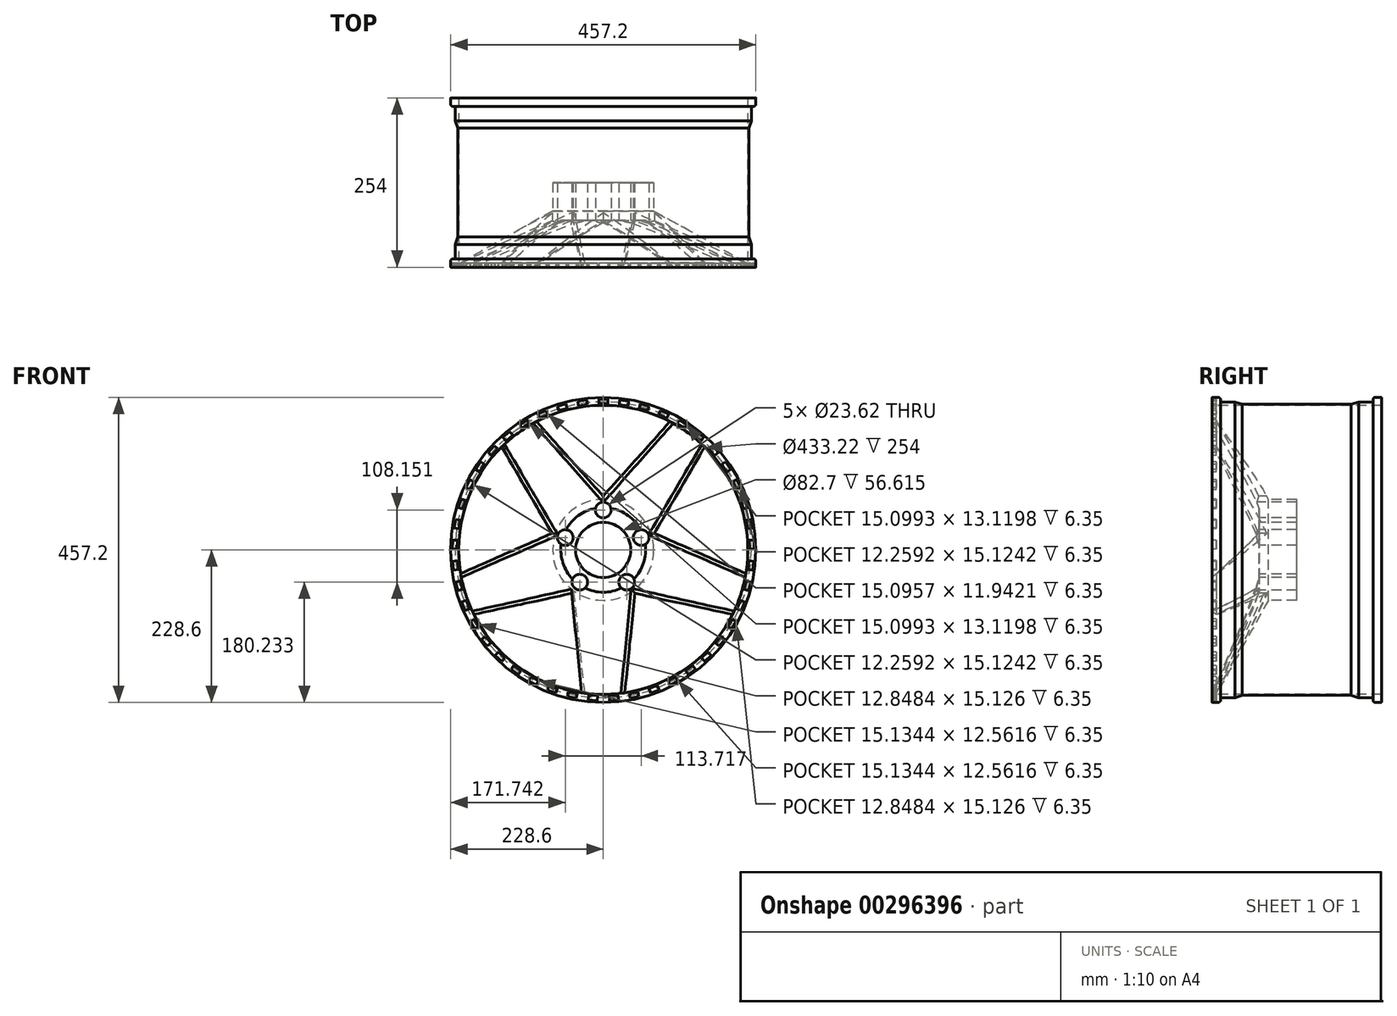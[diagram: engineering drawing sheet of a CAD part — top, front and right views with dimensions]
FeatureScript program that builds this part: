
annotation { "Feature Type Name" : "Feature", "Feature Type Description" : "" }
export const myFeature = defineFeature(function(context is Context, id is Id, definition is map)
    precondition{}
    {
        {
            var Q0;
            Q0=qCreatedBy(makeId("Right.planeOp"),FACE);
            var sketch = newSketch(context, id + "F0", { "sketchPlane" : qUnion([Q0])});
            skLineSegment(sketch, "E0", {"start": v(0, 0) * mm, "end": v(-56.62, 0) * mm});
            skLineSegment(sketch, "E1", {"start": v(0, 0) * mm, "end": v(0, 75.72) * mm});
            skLineSegment(sketch, "E2", {"start": v(0, 0) * mm, "end": v(0, 63.5) * mm});
            skLineSegment(sketch, "E3", {"start": v(-127, 216.61) * mm, "end": v(-127, 228.28) * mm});
            skLineSegment(sketch, "E4", {"start": v(-126.68, 228.6) * mm, "end": v(-117.48, 228.6) * mm});
            skLineSegment(sketch, "E5", {"start": v(-127, 216.61) * mm, "end": v(-56.62, 63.5) * mm});
            skLineSegment(sketch, "E6", {"start": v(-120.38, 216.61) * mm, "end": v(-42.61, 75.72) * mm});
            skLineSegment(sketch, "E7", {"start": v(-120.38, 216.61) * mm, "end": v(0, 216.61) * mm});
            skLineSegment(sketch, "E8", {"start": v(-114.3, 225.43) * mm, "end": v(-114.3, 223.38) * mm});
            skLineSegment(sketch, "E9", {"start": v(-112.78, 221.86) * mm, "end": v(-92.74, 221.86) * mm});
            skLineSegment(sketch, "E10", {"start": v(-92.74, 221.86) * mm, "end": v(-81.66, 218.09) * mm});
            skLineSegment(sketch, "E11", {"start": v(-81.66, 218.09) * mm, "end": v(0, 218.09) * mm});
            skPoint(sketch, "E12.visualSharp", {"position": v(-127, 228.6) * mm});
            skArc(sketch, "E12.filletArc", {"start": v(-126.68, 228.6) * mm, "mid": v(-126.9, 228.5) * mm, "end": v(-127, 228.28) * mm});
            skPoint(sketch, "E13.visualSharp", {"position": v(-114.3, 228.6) * mm});
            skArc(sketch, "E13.filletArc", {"start": v(-114.3, 225.43) * mm, "mid": v(-115.23, 227.67) * mm, "end": v(-117.48, 228.6) * mm});
            skPoint(sketch, "E14.visualSharp", {"position": v(-114.3, 221.86) * mm});
            skArc(sketch, "E14.filletArc", {"start": v(-114.3, 223.38) * mm, "mid": v(-113.85, 222.3) * mm, "end": v(-112.78, 221.86) * mm});
            skLineSegment(sketch, "E15", {"start": v(-56.62, 63.5) * mm, "end": v(-56.62, 0) * mm});
            skLineSegment(sketch, "E16", {"start": v(-56.62, 0) * mm, "end": v(0, 0) * mm});
            skLineSegment(sketch, "E17", {"start": v(-42.61, 75.72) * mm, "end": v(0, 75.72) * mm});
            skLineSegment(sketch, "E18", {"start": v(0, 75.72) * mm, "end": v(0, 63.5) * mm});
            skPoint(sketch, "E19.orphan", {"position": v(-35.86, 63.5) * mm});
            skPoint(sketch, "E20.orphan", {"position": v(0, 228.6) * mm});
            skLineSegment(sketch, "E21.MirrorCS", {"start": v(120.38, 216.61) * mm, "end": v(0, 216.61) * mm});
            skLineSegment(sketch, "E22.MirrorCS", {"start": v(127, 216.61) * mm, "end": v(127, 228.28) * mm});
            skLineSegment(sketch, "E23.MirrorCS", {"start": v(81.66, 218.09) * mm, "end": v(0, 218.09) * mm});
            skLineSegment(sketch, "E24.MirrorCS", {"start": v(92.74, 221.86) * mm, "end": v(81.66, 218.09) * mm});
            skLineSegment(sketch, "E25.MirrorCS", {"start": v(112.78, 221.86) * mm, "end": v(92.74, 221.86) * mm});
            skLineSegment(sketch, "E26.MirrorCS", {"start": v(126.68, 228.6) * mm, "end": v(117.48, 228.6) * mm});
            skArc(sketch, "E27.MirrorCS", {"start": v(114.3, 225.43) * mm, "mid": v(115.23, 227.67) * mm, "end": v(117.48, 228.6) * mm});
            skLineSegment(sketch, "E28.MirrorCS", {"start": v(114.3, 225.43) * mm, "end": v(114.3, 223.38) * mm});
            skArc(sketch, "E29.MirrorCS", {"start": v(114.3, 223.38) * mm, "mid": v(113.85, 222.3) * mm, "end": v(112.78, 221.86) * mm});
            skArc(sketch, "E30.MirrorCS", {"start": v(126.68, 228.6) * mm, "mid": v(126.9, 228.5) * mm, "end": v(127, 228.28) * mm});
            skLineSegment(sketch, "E31", {"start": v(127, 216.61) * mm, "end": v(120.38, 216.61) * mm});
            skLineSegment(sketch, "E32", {"start": v(-76.11, 0) * mm, "end": v(62.35, 0) * mm});
            skSolve(sketch);
        }
        {
            var Q0;
            Q0 = qSketchRegion(id + "F0", true);
            var Q1;
            Q1=sQuery(id+"F0.wireOp",EDGE,"E32");
            revolve(context, id + "F1", {"entities" : qUnion([Q0]), "axis" : qUnion([Q1]), "revolveType" : RevolveType.FULL});
        }
        {
            var Q0;
            Q0=makeQuery(id+"F1.opRevolve","SWEPT_FACE",FACE,{"disambiguationData":[OSD([sQuery(id+"F0.wireOp",EDGE,"E3")])]});
            var sketch = newSketch(context, id + "F2", { "sketchPlane" : qUnion([Q0])});
            skCircle(sketch, "E33", {"center": v(0, 59.78) * mm, "radius": 11.8 * mm});
            skCircle(sketch, "E34.1.0", {"center": v(-56.86, 18.47) * mm, "radius": 11.8 * mm});
            skCircle(sketch, "E34.2.0", {"center": v(-35.14, -48.37) * mm, "radius": 11.8 * mm});
            skCircle(sketch, "E34.3.0", {"center": v(35.14, -48.37) * mm, "radius": 11.8 * mm});
            skCircle(sketch, "E34.4.0", {"center": v(56.86, 18.47) * mm, "radius": 11.8 * mm});
            skPoint(sketch, "E34.center", {"position": v(0, 0) * mm});
            skCircle(sketch, "E35", {"center": v(0, 0) * mm, "radius": 41.35 * mm});
            skPoint(sketch, "E36.0.midPoint", {"position": v(0, -65.14) * mm});
            skLineSegment(sketch, "E37", {"start": v(47.33, -65.14) * mm, "end": v(32.25, -214.2) * mm});
            skLineSegment(sketch, "E38.MirrorCS", {"start": v(-47.33, -65.14) * mm, "end": v(-32.25, -214.2) * mm});
            skLineSegment(sketch, "E39.1.0", {"start": v(47.33, -65.14) * mm, "end": v(193.75, -96.86) * mm});
            skLineSegment(sketch, "E39.1.1", {"start": v(76.57, 24.88) * mm, "end": v(213.68, -35.52) * mm});
            skLineSegment(sketch, "E39.2.0", {"start": v(76.57, 24.88) * mm, "end": v(152, 154.33) * mm});
            skLineSegment(sketch, "E39.2.1", {"start": v(0, 80.52) * mm, "end": v(99.81, 192.24) * mm});
            skLineSegment(sketch, "E39.3.0", {"start": v(0, 80.52) * mm, "end": v(-99.81, 192.24) * mm});
            skLineSegment(sketch, "E39.3.1", {"start": v(-76.57, 24.88) * mm, "end": v(-152, 154.33) * mm});
            skLineSegment(sketch, "E39.4.0", {"start": v(-76.57, 24.88) * mm, "end": v(-213.68, -35.52) * mm});
            skLineSegment(sketch, "E39.4.1", {"start": v(-47.33, -65.14) * mm, "end": v(-193.75, -96.86) * mm});
            skArc(sketch, "E40", {"start": v(-152, 154.33) * mm, "mid": v(-206, 66.94) * mm, "end": v(-213.68, -35.52) * mm});
            skArc(sketch, "E41.trimOffspring", {"start": v(99.81, 192.24) * mm, "mid": v(0, 216.61) * mm, "end": v(-99.81, 192.24) * mm});
            skArc(sketch, "E42.trimOffspring", {"start": v(213.68, -35.52) * mm, "mid": v(206, 66.94) * mm, "end": v(152, 154.33) * mm});
            skArc(sketch, "E43.trimOffspring", {"start": v(32.25, -214.2) * mm, "mid": v(127.32, -175.24) * mm, "end": v(193.75, -96.86) * mm});
            skArc(sketch, "E44.trimOffspring", {"start": v(-193.75, -96.86) * mm, "mid": v(-127.32, -175.24) * mm, "end": v(-32.25, -214.2) * mm});
            skPoint(sketch, "E45.orphan", {"position": v(-76.57, 24.88) * mm});
            skPoint(sketch, "E36.1.start.orphan", {"position": v(-47.33, -65.14) * mm});
            skSolve(sketch);
        }
        {
            var Q0;
            Q0 = qSketchRegion(id + "F2", true);
            extrude(context, id + "F3", {"entities" : qUnion([Q0]), "operationType" : NewBodyOperationType.REMOVE, "endBound" : BoundingType.THROUGH_ALL, "oppositeDirection" : true, "depth" : 25.4 * mm});
        }
        {
            var Q0;
            Q0=makeQuery(id+"F3.boolean.opBoolean","INTERSECT",EDGE,{"derivedFrom":[makeQuery(id+"F1.opRevolve","SWEPT_FACE",FACE,{"disambiguationData":[OSD([sQuery(id+"F0.wireOp",EDGE,"E5")])]}),makeQuery(id+"F3.opExtrude","SWEPT_FACE",FACE,{"disambiguationData":[OSD([sQuery(id+"F2.wireOp",EDGE,"E39.1.0")])]})]});
            var Q1;
            Q1=makeQuery(id+"F3.boolean.opBoolean","INTERSECT",EDGE,{"derivedFrom":[makeQuery(id+"F1.opRevolve","SWEPT_FACE",FACE,{"disambiguationData":[OSD([sQuery(id+"F0.wireOp",EDGE,"E5")])]}),makeQuery(id+"F3.opExtrude","SWEPT_FACE",FACE,{"disambiguationData":[OSD([sQuery(id+"F2.wireOp",EDGE,"E37")])]})]});
            var Q2;
            Q2=makeQuery(id+"F3.boolean.opBoolean","INTERSECT",EDGE,{"derivedFrom":[makeQuery(id+"F1.opRevolve","SWEPT_FACE",FACE,{"disambiguationData":[OSD([sQuery(id+"F0.wireOp",EDGE,"E6")])]}),makeQuery(id+"F3.opExtrude","SWEPT_FACE",FACE,{"disambiguationData":[OSD([sQuery(id+"F2.wireOp",EDGE,"E38.MirrorCS")])]})]});
            var Q3;
            Q3=makeQuery(id+"F3.boolean.opBoolean","INTERSECT",EDGE,{"derivedFrom":[makeQuery(id+"F1.opRevolve","SWEPT_FACE",FACE,{"disambiguationData":[OSD([sQuery(id+"F0.wireOp",EDGE,"E5")])]}),makeQuery(id+"F3.opExtrude","SWEPT_FACE",FACE,{"disambiguationData":[OSD([sQuery(id+"F2.wireOp",EDGE,"E39.4.1")])]})]});
            var Q4;
            Q4=makeQuery(id+"F3.boolean.opBoolean","INTERSECT",EDGE,{"derivedFrom":[makeQuery(id+"F1.opRevolve","SWEPT_FACE",FACE,{"disambiguationData":[OSD([sQuery(id+"F0.wireOp",EDGE,"E5")])]}),makeQuery(id+"F3.opExtrude","SWEPT_FACE",FACE,{"disambiguationData":[OSD([sQuery(id+"F2.wireOp",EDGE,"E39.4.0")])]})]});
            var Q5;
            Q5=makeQuery(id+"F3.boolean.opBoolean","INTERSECT",EDGE,{"derivedFrom":[makeQuery(id+"F1.opRevolve","SWEPT_FACE",FACE,{"disambiguationData":[OSD([sQuery(id+"F0.wireOp",EDGE,"E5")])]}),makeQuery(id+"F3.opExtrude","SWEPT_FACE",FACE,{"disambiguationData":[OSD([sQuery(id+"F2.wireOp",EDGE,"E39.3.1")])]})]});
            var Q6;
            Q6=makeQuery(id+"F3.boolean.opBoolean","INTERSECT",EDGE,{"derivedFrom":[makeQuery(id+"F1.opRevolve","SWEPT_FACE",FACE,{"disambiguationData":[OSD([sQuery(id+"F0.wireOp",EDGE,"E5")])]}),makeQuery(id+"F3.opExtrude","SWEPT_FACE",FACE,{"disambiguationData":[OSD([sQuery(id+"F2.wireOp",EDGE,"E39.3.0")])]})]});
            var Q7;
            Q7=makeQuery(id+"F3.boolean.opBoolean","INTERSECT",EDGE,{"derivedFrom":[makeQuery(id+"F1.opRevolve","SWEPT_FACE",FACE,{"disambiguationData":[OSD([sQuery(id+"F0.wireOp",EDGE,"E5")])]}),makeQuery(id+"F3.opExtrude","SWEPT_FACE",FACE,{"disambiguationData":[OSD([sQuery(id+"F2.wireOp",EDGE,"E39.2.1")])]})]});
            var Q8;
            Q8=makeQuery(id+"F3.boolean.opBoolean","INTERSECT",EDGE,{"derivedFrom":[makeQuery(id+"F1.opRevolve","SWEPT_FACE",FACE,{"disambiguationData":[OSD([sQuery(id+"F0.wireOp",EDGE,"E5")])]}),makeQuery(id+"F3.opExtrude","SWEPT_FACE",FACE,{"disambiguationData":[OSD([sQuery(id+"F2.wireOp",EDGE,"E39.2.0")])]})]});
            var Q9;
            Q9=makeQuery(id+"F3.boolean.opBoolean","INTERSECT",EDGE,{"derivedFrom":[makeQuery(id+"F1.opRevolve","SWEPT_FACE",FACE,{"disambiguationData":[OSD([sQuery(id+"F0.wireOp",EDGE,"E5")])]}),makeQuery(id+"F3.opExtrude","SWEPT_FACE",FACE,{"disambiguationData":[OSD([sQuery(id+"F2.wireOp",EDGE,"E39.1.1")])]})]});
            chamfer(context, id + "F4", {"entities" : qUnion([Q0, Q1, Q2, Q3, Q4, Q5, Q6, Q7, Q8, Q9]), "width" : 5.08 * mm, "tangentPropagation" : true});
        }
        {
            var Q0;
            Q0=makeQuery(id+"F1.opRevolve","SWEPT_FACE",FACE,{"disambiguationData":[OSD([sQuery(id+"F0.wireOp",EDGE,"E3")])]});
            var sketch = newSketch(context, id + "F5", { "sketchPlane" : qUnion([Q0])});
            skPoint(sketch, "E46.endSnap0", {"position": v(0, 216.61) * mm});
            skLineSegment(sketch, "E47", {"start": v(0, 218.86) * mm, "end": v(6.68, 218.86) * mm});
            skLineSegment(sketch, "E48", {"start": v(6.68, 218.86) * mm, "end": v(6.68, 226) * mm});
            skLineSegment(sketch, "E49", {"start": v(6.68, 226) * mm, "end": v(0, 226) * mm});
            skLineSegment(sketch, "E50.MirrorCS", {"start": v(-6.68, 226) * mm, "end": v(0, 226) * mm});
            skLineSegment(sketch, "E51.MirrorCS", {"start": v(-6.68, 218.86) * mm, "end": v(-6.68, 226) * mm});
            skLineSegment(sketch, "E52.MirrorCS", {"start": v(0, 218.86) * mm, "end": v(-6.68, 218.86) * mm});
            skPoint(sketch, "E53.orphan", {"position": v(0, 222) * mm});
            skLineSegment(sketch, "E54.1.0", {"start": v(-38.06, 222.86) * mm, "end": v(-31.45, 223.8) * mm});
            skLineSegment(sketch, "E54.1.1", {"start": v(-24.84, 224.72) * mm, "end": v(-31.45, 223.8) * mm});
            skLineSegment(sketch, "E54.1.2", {"start": v(-23.85, 217.66) * mm, "end": v(-24.84, 224.72) * mm});
            skLineSegment(sketch, "E54.1.3", {"start": v(-30.46, 216.73) * mm, "end": v(-23.85, 217.66) * mm});
            skLineSegment(sketch, "E54.1.4", {"start": v(-30.46, 216.73) * mm, "end": v(-37.07, 215.8) * mm});
            skLineSegment(sketch, "E54.1.5", {"start": v(-37.07, 215.8) * mm, "end": v(-38.06, 222.86) * mm});
            skLineSegment(sketch, "E54.2.0", {"start": v(-68.7, 215.4) * mm, "end": v(-62.3, 217.24) * mm});
            skLineSegment(sketch, "E54.2.1", {"start": v(-55.88, 219.08) * mm, "end": v(-62.3, 217.24) * mm});
            skLineSegment(sketch, "E54.2.2", {"start": v(-53.91, 212.23) * mm, "end": v(-55.88, 219.08) * mm});
            skLineSegment(sketch, "E54.2.3", {"start": v(-60.33, 210.39) * mm, "end": v(-53.91, 212.23) * mm});
            skLineSegment(sketch, "E54.2.4", {"start": v(-60.33, 210.39) * mm, "end": v(-66.74, 208.55) * mm});
            skLineSegment(sketch, "E54.2.5", {"start": v(-66.74, 208.55) * mm, "end": v(-68.7, 215.4) * mm});
            skLineSegment(sketch, "E54.3.0", {"start": v(-98.02, 203.74) * mm, "end": v(-91.92, 206.46) * mm});
            skLineSegment(sketch, "E54.3.1", {"start": v(-85.82, 209.17) * mm, "end": v(-91.92, 206.46) * mm});
            skLineSegment(sketch, "E54.3.2", {"start": v(-82.92, 202.66) * mm, "end": v(-85.82, 209.17) * mm});
            skLineSegment(sketch, "E54.3.3", {"start": v(-89.02, 199.94) * mm, "end": v(-82.92, 202.66) * mm});
            skLineSegment(sketch, "E54.3.4", {"start": v(-89.02, 199.94) * mm, "end": v(-95.12, 197.23) * mm});
            skLineSegment(sketch, "E54.3.5", {"start": v(-95.12, 197.23) * mm, "end": v(-98.02, 203.74) * mm});
            skLineSegment(sketch, "E54.4.0", {"start": v(-125.42, 188.12) * mm, "end": v(-119.76, 191.65) * mm});
            skLineSegment(sketch, "E54.4.1", {"start": v(-114.1, 195.2) * mm, "end": v(-119.76, 191.65) * mm});
            skLineSegment(sketch, "E54.4.2", {"start": v(-110.32, 189.15) * mm, "end": v(-114.1, 195.2) * mm});
            skLineSegment(sketch, "E54.4.3", {"start": v(-115.98, 185.6) * mm, "end": v(-110.32, 189.15) * mm});
            skLineSegment(sketch, "E54.4.4", {"start": v(-115.98, 185.6) * mm, "end": v(-121.64, 182.07) * mm});
            skLineSegment(sketch, "E54.4.5", {"start": v(-121.64, 182.07) * mm, "end": v(-125.42, 188.12) * mm});
            skLineSegment(sketch, "E54.5.0", {"start": v(-150.38, 168.83) * mm, "end": v(-145.27, 173.12) * mm});
            skLineSegment(sketch, "E54.5.1", {"start": v(-140.15, 177.41) * mm, "end": v(-145.27, 173.12) * mm});
            skLineSegment(sketch, "E54.5.2", {"start": v(-135.57, 171.95) * mm, "end": v(-140.15, 177.41) * mm});
            skLineSegment(sketch, "E54.5.3", {"start": v(-140.68, 167.66) * mm, "end": v(-135.57, 171.95) * mm});
            skLineSegment(sketch, "E54.5.4", {"start": v(-140.68, 167.66) * mm, "end": v(-145.8, 163.37) * mm});
            skLineSegment(sketch, "E54.5.5", {"start": v(-145.8, 163.37) * mm, "end": v(-150.38, 168.83) * mm});
            skLineSegment(sketch, "E54.6.0", {"start": v(-172.41, 146.26) * mm, "end": v(-167.95, 151.22) * mm});
            skLineSegment(sketch, "E54.6.1", {"start": v(-163.48, 156.18) * mm, "end": v(-167.95, 151.22) * mm});
            skLineSegment(sketch, "E54.6.2", {"start": v(-158.18, 151.4) * mm, "end": v(-163.48, 156.18) * mm});
            skLineSegment(sketch, "E54.6.3", {"start": v(-162.65, 146.45) * mm, "end": v(-158.18, 151.4) * mm});
            skLineSegment(sketch, "E54.6.4", {"start": v(-162.65, 146.45) * mm, "end": v(-167.12, 141.49) * mm});
            skLineSegment(sketch, "E54.6.5", {"start": v(-167.12, 141.49) * mm, "end": v(-172.41, 146.26) * mm});
            skLineSegment(sketch, "E54.7.0", {"start": v(-191.09, 120.84) * mm, "end": v(-187.36, 126.37) * mm});
            skLineSegment(sketch, "E54.7.1", {"start": v(-183.62, 131.9) * mm, "end": v(-187.36, 126.37) * mm});
            skLineSegment(sketch, "E54.7.2", {"start": v(-177.71, 127.92) * mm, "end": v(-183.62, 131.9) * mm});
            skLineSegment(sketch, "E54.7.3", {"start": v(-181.45, 122.39) * mm, "end": v(-177.71, 127.92) * mm});
            skLineSegment(sketch, "E54.7.4", {"start": v(-181.45, 122.39) * mm, "end": v(-185.18, 116.85) * mm});
            skLineSegment(sketch, "E54.7.5", {"start": v(-185.18, 116.85) * mm, "end": v(-191.09, 120.84) * mm});
            skLineSegment(sketch, "E54.8.0", {"start": v(-206.05, 93.07) * mm, "end": v(-203.12, 99.07) * mm});
            skLineSegment(sketch, "E54.8.1", {"start": v(-200.2, 105.07) * mm, "end": v(-203.12, 99.07) * mm});
            skLineSegment(sketch, "E54.8.2", {"start": v(-193.79, 101.94) * mm, "end": v(-200.2, 105.07) * mm});
            skLineSegment(sketch, "E54.8.3", {"start": v(-196.71, 95.94) * mm, "end": v(-193.79, 101.94) * mm});
            skLineSegment(sketch, "E54.8.4", {"start": v(-196.71, 95.94) * mm, "end": v(-199.64, 89.94) * mm});
            skLineSegment(sketch, "E54.8.5", {"start": v(-199.64, 89.94) * mm, "end": v(-206.05, 93.07) * mm});
            skLineSegment(sketch, "E54.9.0", {"start": v(-217, 63.49) * mm, "end": v(-214.93, 69.84) * mm});
            skLineSegment(sketch, "E54.9.1", {"start": v(-212.87, 76.18) * mm, "end": v(-214.93, 69.84) * mm});
            skLineSegment(sketch, "E54.9.2", {"start": v(-206.1, 73.98) * mm, "end": v(-212.87, 76.18) * mm});
            skLineSegment(sketch, "E54.9.3", {"start": v(-208.15, 67.63) * mm, "end": v(-206.1, 73.98) * mm});
            skLineSegment(sketch, "E54.9.4", {"start": v(-208.15, 67.63) * mm, "end": v(-210.22, 61.28) * mm});
            skLineSegment(sketch, "E54.9.5", {"start": v(-210.22, 61.28) * mm, "end": v(-217, 63.49) * mm});
            skLineSegment(sketch, "E54.10.0", {"start": v(-223.72, 32.67) * mm, "end": v(-222.56, 39.24) * mm});
            skLineSegment(sketch, "E54.10.1", {"start": v(-221.4, 45.82) * mm, "end": v(-222.56, 39.24) * mm});
            skLineSegment(sketch, "E54.10.2", {"start": v(-214.38, 44.58) * mm, "end": v(-221.4, 45.82) * mm});
            skLineSegment(sketch, "E54.10.3", {"start": v(-215.54, 38) * mm, "end": v(-214.38, 44.58) * mm});
            skLineSegment(sketch, "E54.10.4", {"start": v(-215.54, 38) * mm, "end": v(-216.7, 31.43) * mm});
            skLineSegment(sketch, "E54.10.5", {"start": v(-216.7, 31.43) * mm, "end": v(-223.72, 32.67) * mm});
            skLineSegment(sketch, "E54.11.0", {"start": v(-226.09, 1.22) * mm, "end": v(-225.86, 7.89) * mm});
            skLineSegment(sketch, "E54.11.1", {"start": v(-225.62, 14.56) * mm, "end": v(-225.86, 7.89) * mm});
            skLineSegment(sketch, "E54.11.2", {"start": v(-218.5, 14.3) * mm, "end": v(-225.62, 14.56) * mm});
            skLineSegment(sketch, "E54.11.3", {"start": v(-218.73, 7.64) * mm, "end": v(-218.5, 14.3) * mm});
            skLineSegment(sketch, "E54.11.4", {"start": v(-218.73, 7.64) * mm, "end": v(-218.96, 0.97) * mm});
            skLineSegment(sketch, "E54.11.5", {"start": v(-218.96, 0.97) * mm, "end": v(-226.09, 1.22) * mm});
            skLineSegment(sketch, "E54.12.0", {"start": v(-224.06, -30.26) * mm, "end": v(-224.76, -23.62) * mm});
            skLineSegment(sketch, "E54.12.1", {"start": v(-225.45, -16.98) * mm, "end": v(-224.76, -23.62) * mm});
            skLineSegment(sketch, "E54.12.2", {"start": v(-218.36, -16.24) * mm, "end": v(-225.45, -16.98) * mm});
            skLineSegment(sketch, "E54.12.3", {"start": v(-217.67, -22.88) * mm, "end": v(-218.36, -16.24) * mm});
            skLineSegment(sketch, "E54.12.4", {"start": v(-217.67, -22.88) * mm, "end": v(-216.97, -29.52) * mm});
            skLineSegment(sketch, "E54.12.5", {"start": v(-216.97, -29.52) * mm, "end": v(-224.06, -30.26) * mm});
            skLineSegment(sketch, "E54.13.0", {"start": v(-217.67, -61.15) * mm, "end": v(-219.28, -54.67) * mm});
            skLineSegment(sketch, "E54.13.1", {"start": v(-220.9, -48.2) * mm, "end": v(-219.28, -54.67) * mm});
            skLineSegment(sketch, "E54.13.2", {"start": v(-213.98, -46.47) * mm, "end": v(-220.9, -48.2) * mm});
            skLineSegment(sketch, "E54.13.3", {"start": v(-212.36, -52.95) * mm, "end": v(-213.98, -46.47) * mm});
            skLineSegment(sketch, "E54.13.4", {"start": v(-212.36, -52.95) * mm, "end": v(-210.75, -59.43) * mm});
            skLineSegment(sketch, "E54.13.5", {"start": v(-210.75, -59.43) * mm, "end": v(-217.67, -61.15) * mm});
            skLineSegment(sketch, "E54.14.0", {"start": v(-207.04, -90.85) * mm, "end": v(-209.54, -84.66) * mm});
            skLineSegment(sketch, "E54.14.1", {"start": v(-212.04, -78.47) * mm, "end": v(-209.54, -84.66) * mm});
            skLineSegment(sketch, "E54.14.2", {"start": v(-205.43, -75.8) * mm, "end": v(-212.04, -78.47) * mm});
            skLineSegment(sketch, "E54.14.3", {"start": v(-202.93, -81.99) * mm, "end": v(-205.43, -75.8) * mm});
            skLineSegment(sketch, "E54.14.4", {"start": v(-202.93, -81.99) * mm, "end": v(-200.43, -88.18) * mm});
            skLineSegment(sketch, "E54.14.5", {"start": v(-200.43, -88.18) * mm, "end": v(-207.04, -90.85) * mm});
            skLineSegment(sketch, "E54.15.0", {"start": v(-192.38, -118.78) * mm, "end": v(-195.72, -113) * mm});
            skLineSegment(sketch, "E54.15.1", {"start": v(-199.05, -107.22) * mm, "end": v(-195.72, -113) * mm});
            skLineSegment(sketch, "E54.15.2", {"start": v(-192.88, -103.65) * mm, "end": v(-199.05, -107.22) * mm});
            skLineSegment(sketch, "E54.15.3", {"start": v(-189.54, -109.43) * mm, "end": v(-192.88, -103.65) * mm});
            skLineSegment(sketch, "E54.15.4", {"start": v(-189.54, -109.43) * mm, "end": v(-186.2, -115.21) * mm});
            skLineSegment(sketch, "E54.15.5", {"start": v(-186.2, -115.21) * mm, "end": v(-192.38, -118.78) * mm});
            skLineSegment(sketch, "E54.16.0", {"start": v(-173.98, -144.4) * mm, "end": v(-178.09, -139.14) * mm});
            skLineSegment(sketch, "E54.16.1", {"start": v(-182.2, -133.88) * mm, "end": v(-178.09, -139.14) * mm});
            skLineSegment(sketch, "E54.16.2", {"start": v(-176.58, -129.49) * mm, "end": v(-182.2, -133.88) * mm});
            skLineSegment(sketch, "E54.16.3", {"start": v(-172.47, -134.75) * mm, "end": v(-176.58, -129.49) * mm});
            skLineSegment(sketch, "E54.16.4", {"start": v(-172.47, -134.75) * mm, "end": v(-168.36, -140) * mm});
            skLineSegment(sketch, "E54.16.5", {"start": v(-168.36, -140) * mm, "end": v(-173.98, -144.4) * mm});
            skLineSegment(sketch, "E54.17.0", {"start": v(-152.19, -167.2) * mm, "end": v(-156.99, -162.57) * mm});
            skLineSegment(sketch, "E54.17.1", {"start": v(-161.79, -157.93) * mm, "end": v(-156.99, -162.57) * mm});
            skLineSegment(sketch, "E54.17.2", {"start": v(-156.84, -152.8) * mm, "end": v(-161.79, -157.93) * mm});
            skLineSegment(sketch, "E54.17.3", {"start": v(-152.04, -157.44) * mm, "end": v(-156.84, -152.8) * mm});
            skLineSegment(sketch, "E54.17.4", {"start": v(-152.04, -157.44) * mm, "end": v(-147.23, -162.08) * mm});
            skLineSegment(sketch, "E54.17.5", {"start": v(-147.23, -162.08) * mm, "end": v(-152.19, -167.2) * mm});
            skLineSegment(sketch, "E54.18.0", {"start": v(-127.44, -186.76) * mm, "end": v(-132.84, -182.83) * mm});
            skLineSegment(sketch, "E54.18.1", {"start": v(-138.24, -178.9) * mm, "end": v(-132.84, -182.83) * mm});
            skLineSegment(sketch, "E54.18.2", {"start": v(-134.05, -173.14) * mm, "end": v(-138.24, -178.9) * mm});
            skLineSegment(sketch, "E54.18.3", {"start": v(-128.65, -177.07) * mm, "end": v(-134.05, -173.14) * mm});
            skLineSegment(sketch, "E54.18.4", {"start": v(-128.65, -177.07) * mm, "end": v(-123.25, -180.99) * mm});
            skLineSegment(sketch, "E54.18.5", {"start": v(-123.25, -180.99) * mm, "end": v(-127.44, -186.76) * mm});
            skLineSegment(sketch, "E54.19.0", {"start": v(-100.2, -202.67) * mm, "end": v(-106.1, -199.54) * mm});
            skLineSegment(sketch, "E54.19.1", {"start": v(-112, -196.4) * mm, "end": v(-106.1, -199.54) * mm});
            skLineSegment(sketch, "E54.19.2", {"start": v(-108.64, -190.11) * mm, "end": v(-112, -196.4) * mm});
            skLineSegment(sketch, "E54.19.3", {"start": v(-102.75, -193.25) * mm, "end": v(-108.64, -190.11) * mm});
            skLineSegment(sketch, "E54.19.4", {"start": v(-102.75, -193.25) * mm, "end": v(-96.86, -196.38) * mm});
            skLineSegment(sketch, "E54.19.5", {"start": v(-96.86, -196.38) * mm, "end": v(-100.2, -202.67) * mm});
            skPoint(sketch, "E54.center", {"position": v(0, 0) * mm});
            skLineSegment(sketch, "E55.1.20.0", {"start": v(-71.02, -214.65) * mm, "end": v(-77.3, -212.36) * mm});
            skLineSegment(sketch, "E55.3.20.0", {"start": v(-83.57, -210.08) * mm, "end": v(-77.3, -212.36) * mm});
            skLineSegment(sketch, "E55.6.20.0", {"start": v(-81.13, -203.38) * mm, "end": v(-83.57, -210.08) * mm});
            skLineSegment(sketch, "E55.9.20.0", {"start": v(-74.86, -205.67) * mm, "end": v(-81.13, -203.38) * mm});
            skLineSegment(sketch, "E55.12.20.0", {"start": v(-74.86, -205.67) * mm, "end": v(-68.58, -207.95) * mm});
            skLineSegment(sketch, "E55.15.20.0", {"start": v(-68.58, -207.95) * mm, "end": v(-71.02, -214.65) * mm});
            skLineSegment(sketch, "E55.1.21.0", {"start": v(-40.46, -222.44) * mm, "end": v(-46.99, -221.05) * mm});
            skLineSegment(sketch, "E55.3.21.0", {"start": v(-53.52, -219.67) * mm, "end": v(-46.99, -221.05) * mm});
            skLineSegment(sketch, "E55.6.21.0", {"start": v(-52.03, -212.7) * mm, "end": v(-53.52, -219.67) * mm});
            skLineSegment(sketch, "E55.9.21.0", {"start": v(-45.5, -214.08) * mm, "end": v(-52.03, -212.7) * mm});
            skLineSegment(sketch, "E55.12.21.0", {"start": v(-45.5, -214.08) * mm, "end": v(-38.98, -215.47) * mm});
            skLineSegment(sketch, "E55.15.21.0", {"start": v(-38.98, -215.47) * mm, "end": v(-40.46, -222.44) * mm});
            skLineSegment(sketch, "E55.1.22.0", {"start": v(-9.1, -225.9) * mm, "end": v(-15.76, -225.44) * mm});
            skLineSegment(sketch, "E55.3.22.0", {"start": v(-22.42, -224.98) * mm, "end": v(-15.76, -225.44) * mm});
            skLineSegment(sketch, "E55.6.22.0", {"start": v(-21.93, -217.87) * mm, "end": v(-22.42, -224.98) * mm});
            skLineSegment(sketch, "E55.9.22.0", {"start": v(-15.27, -218.33) * mm, "end": v(-21.93, -217.87) * mm});
            skLineSegment(sketch, "E55.12.22.0", {"start": v(-15.27, -218.33) * mm, "end": v(-8.6, -218.8) * mm});
            skLineSegment(sketch, "E55.15.22.0", {"start": v(-8.6, -218.8) * mm, "end": v(-9.1, -225.9) * mm});
            skLineSegment(sketch, "E55.1.23.0", {"start": v(22.42, -224.98) * mm, "end": v(15.76, -225.44) * mm});
            skLineSegment(sketch, "E55.3.23.0", {"start": v(9.1, -225.9) * mm, "end": v(15.76, -225.44) * mm});
            skLineSegment(sketch, "E55.6.23.0", {"start": v(8.6, -218.8) * mm, "end": v(9.1, -225.9) * mm});
            skLineSegment(sketch, "E55.9.23.0", {"start": v(15.27, -218.33) * mm, "end": v(8.6, -218.8) * mm});
            skLineSegment(sketch, "E55.12.23.0", {"start": v(15.27, -218.33) * mm, "end": v(21.93, -217.87) * mm});
            skLineSegment(sketch, "E55.15.23.0", {"start": v(21.93, -217.87) * mm, "end": v(22.42, -224.98) * mm});
            skLineSegment(sketch, "E55.1.24.0", {"start": v(53.52, -219.67) * mm, "end": v(46.99, -221.05) * mm});
            skLineSegment(sketch, "E55.3.24.0", {"start": v(40.46, -222.44) * mm, "end": v(46.99, -221.05) * mm});
            skLineSegment(sketch, "E55.6.24.0", {"start": v(38.98, -215.47) * mm, "end": v(40.46, -222.44) * mm});
            skLineSegment(sketch, "E55.9.24.0", {"start": v(45.5, -214.08) * mm, "end": v(38.98, -215.47) * mm});
            skLineSegment(sketch, "E55.12.24.0", {"start": v(45.5, -214.08) * mm, "end": v(52.03, -212.7) * mm});
            skLineSegment(sketch, "E55.15.24.0", {"start": v(52.03, -212.7) * mm, "end": v(53.52, -219.67) * mm});
            skLineSegment(sketch, "E55.1.25.0", {"start": v(83.57, -210.08) * mm, "end": v(77.3, -212.36) * mm});
            skLineSegment(sketch, "E55.3.25.0", {"start": v(71.02, -214.65) * mm, "end": v(77.3, -212.36) * mm});
            skLineSegment(sketch, "E55.6.25.0", {"start": v(68.58, -207.95) * mm, "end": v(71.02, -214.65) * mm});
            skLineSegment(sketch, "E55.9.25.0", {"start": v(74.86, -205.67) * mm, "end": v(68.58, -207.95) * mm});
            skLineSegment(sketch, "E55.12.25.0", {"start": v(74.86, -205.67) * mm, "end": v(81.13, -203.38) * mm});
            skLineSegment(sketch, "E55.15.25.0", {"start": v(81.13, -203.38) * mm, "end": v(83.57, -210.08) * mm});
            skLineSegment(sketch, "E55.1.26.0", {"start": v(112, -196.4) * mm, "end": v(106.1, -199.54) * mm});
            skLineSegment(sketch, "E55.3.26.0", {"start": v(100.2, -202.67) * mm, "end": v(106.1, -199.54) * mm});
            skLineSegment(sketch, "E55.6.26.0", {"start": v(96.86, -196.38) * mm, "end": v(100.2, -202.67) * mm});
            skLineSegment(sketch, "E55.9.26.0", {"start": v(102.75, -193.25) * mm, "end": v(96.86, -196.38) * mm});
            skLineSegment(sketch, "E55.12.26.0", {"start": v(102.75, -193.25) * mm, "end": v(108.64, -190.11) * mm});
            skLineSegment(sketch, "E55.15.26.0", {"start": v(108.64, -190.11) * mm, "end": v(112, -196.4) * mm});
            skLineSegment(sketch, "E55.1.27.0", {"start": v(138.24, -178.9) * mm, "end": v(132.84, -182.83) * mm});
            skLineSegment(sketch, "E55.3.27.0", {"start": v(127.44, -186.76) * mm, "end": v(132.84, -182.83) * mm});
            skLineSegment(sketch, "E55.6.27.0", {"start": v(123.25, -180.99) * mm, "end": v(127.44, -186.76) * mm});
            skLineSegment(sketch, "E55.9.27.0", {"start": v(128.65, -177.07) * mm, "end": v(123.25, -180.99) * mm});
            skLineSegment(sketch, "E55.12.27.0", {"start": v(128.65, -177.07) * mm, "end": v(134.05, -173.14) * mm});
            skLineSegment(sketch, "E55.15.27.0", {"start": v(134.05, -173.14) * mm, "end": v(138.24, -178.9) * mm});
            skLineSegment(sketch, "E55.1.28.0", {"start": v(161.79, -157.93) * mm, "end": v(156.99, -162.57) * mm});
            skLineSegment(sketch, "E55.3.28.0", {"start": v(152.19, -167.2) * mm, "end": v(156.99, -162.57) * mm});
            skLineSegment(sketch, "E55.6.28.0", {"start": v(147.23, -162.08) * mm, "end": v(152.19, -167.2) * mm});
            skLineSegment(sketch, "E55.9.28.0", {"start": v(152.04, -157.44) * mm, "end": v(147.23, -162.08) * mm});
            skLineSegment(sketch, "E55.12.28.0", {"start": v(152.04, -157.44) * mm, "end": v(156.84, -152.8) * mm});
            skLineSegment(sketch, "E55.15.28.0", {"start": v(156.84, -152.8) * mm, "end": v(161.79, -157.93) * mm});
            skLineSegment(sketch, "E55.1.29.0", {"start": v(182.2, -133.88) * mm, "end": v(178.09, -139.14) * mm});
            skLineSegment(sketch, "E55.3.29.0", {"start": v(173.98, -144.4) * mm, "end": v(178.09, -139.14) * mm});
            skLineSegment(sketch, "E55.6.29.0", {"start": v(168.36, -140) * mm, "end": v(173.98, -144.4) * mm});
            skLineSegment(sketch, "E55.9.29.0", {"start": v(172.47, -134.75) * mm, "end": v(168.36, -140) * mm});
            skLineSegment(sketch, "E55.12.29.0", {"start": v(172.47, -134.75) * mm, "end": v(176.58, -129.49) * mm});
            skLineSegment(sketch, "E55.15.29.0", {"start": v(176.58, -129.49) * mm, "end": v(182.2, -133.88) * mm});
            skLineSegment(sketch, "E56.1.30.0", {"start": v(199.05, -107.22) * mm, "end": v(195.72, -113) * mm});
            skLineSegment(sketch, "E56.3.30.0", {"start": v(192.38, -118.78) * mm, "end": v(195.72, -113) * mm});
            skLineSegment(sketch, "E56.6.30.0", {"start": v(186.2, -115.21) * mm, "end": v(192.38, -118.78) * mm});
            skLineSegment(sketch, "E56.9.30.0", {"start": v(189.54, -109.43) * mm, "end": v(186.2, -115.21) * mm});
            skLineSegment(sketch, "E56.12.30.0", {"start": v(189.54, -109.43) * mm, "end": v(192.88, -103.65) * mm});
            skLineSegment(sketch, "E56.15.30.0", {"start": v(192.88, -103.65) * mm, "end": v(199.05, -107.22) * mm});
            skLineSegment(sketch, "E56.1.31.0", {"start": v(212.04, -78.47) * mm, "end": v(209.54, -84.66) * mm});
            skLineSegment(sketch, "E56.3.31.0", {"start": v(207.04, -90.85) * mm, "end": v(209.54, -84.66) * mm});
            skLineSegment(sketch, "E56.6.31.0", {"start": v(200.43, -88.18) * mm, "end": v(207.04, -90.85) * mm});
            skLineSegment(sketch, "E56.9.31.0", {"start": v(202.93, -81.99) * mm, "end": v(200.43, -88.18) * mm});
            skLineSegment(sketch, "E56.12.31.0", {"start": v(202.93, -81.99) * mm, "end": v(205.43, -75.8) * mm});
            skLineSegment(sketch, "E56.15.31.0", {"start": v(205.43, -75.8) * mm, "end": v(212.04, -78.47) * mm});
            skLineSegment(sketch, "E56.1.32.0", {"start": v(220.9, -48.2) * mm, "end": v(219.28, -54.67) * mm});
            skLineSegment(sketch, "E56.3.32.0", {"start": v(217.67, -61.15) * mm, "end": v(219.28, -54.67) * mm});
            skLineSegment(sketch, "E56.6.32.0", {"start": v(210.75, -59.43) * mm, "end": v(217.67, -61.15) * mm});
            skLineSegment(sketch, "E56.9.32.0", {"start": v(212.36, -52.95) * mm, "end": v(210.75, -59.43) * mm});
            skLineSegment(sketch, "E56.12.32.0", {"start": v(212.36, -52.95) * mm, "end": v(213.98, -46.47) * mm});
            skLineSegment(sketch, "E56.15.32.0", {"start": v(213.98, -46.47) * mm, "end": v(220.9, -48.2) * mm});
            skLineSegment(sketch, "E56.1.33.0", {"start": v(225.45, -16.98) * mm, "end": v(224.76, -23.62) * mm});
            skLineSegment(sketch, "E56.3.33.0", {"start": v(224.06, -30.26) * mm, "end": v(224.76, -23.62) * mm});
            skLineSegment(sketch, "E56.6.33.0", {"start": v(216.97, -29.52) * mm, "end": v(224.06, -30.26) * mm});
            skLineSegment(sketch, "E56.9.33.0", {"start": v(217.67, -22.88) * mm, "end": v(216.97, -29.52) * mm});
            skLineSegment(sketch, "E56.12.33.0", {"start": v(217.67, -22.88) * mm, "end": v(218.36, -16.24) * mm});
            skLineSegment(sketch, "E56.15.33.0", {"start": v(218.36, -16.24) * mm, "end": v(225.45, -16.98) * mm});
            skLineSegment(sketch, "E56.1.34.0", {"start": v(225.62, 14.56) * mm, "end": v(225.86, 7.89) * mm});
            skLineSegment(sketch, "E56.3.34.0", {"start": v(226.09, 1.22) * mm, "end": v(225.86, 7.89) * mm});
            skLineSegment(sketch, "E56.6.34.0", {"start": v(218.96, 0.97) * mm, "end": v(226.09, 1.22) * mm});
            skLineSegment(sketch, "E56.9.34.0", {"start": v(218.73, 7.64) * mm, "end": v(218.96, 0.97) * mm});
            skLineSegment(sketch, "E56.12.34.0", {"start": v(218.73, 7.64) * mm, "end": v(218.5, 14.3) * mm});
            skLineSegment(sketch, "E56.15.34.0", {"start": v(218.5, 14.3) * mm, "end": v(225.62, 14.56) * mm});
            skLineSegment(sketch, "E57.1.35.0", {"start": v(221.4, 45.82) * mm, "end": v(222.56, 39.24) * mm});
            skLineSegment(sketch, "E57.3.35.0", {"start": v(223.72, 32.67) * mm, "end": v(222.56, 39.24) * mm});
            skLineSegment(sketch, "E57.6.35.0", {"start": v(216.7, 31.43) * mm, "end": v(223.72, 32.67) * mm});
            skLineSegment(sketch, "E57.9.35.0", {"start": v(215.54, 38) * mm, "end": v(216.7, 31.43) * mm});
            skLineSegment(sketch, "E57.12.35.0", {"start": v(215.54, 38) * mm, "end": v(214.38, 44.58) * mm});
            skLineSegment(sketch, "E57.15.35.0", {"start": v(214.38, 44.58) * mm, "end": v(221.4, 45.82) * mm});
            skLineSegment(sketch, "E57.1.36.0", {"start": v(212.87, 76.18) * mm, "end": v(214.93, 69.84) * mm});
            skLineSegment(sketch, "E57.3.36.0", {"start": v(217, 63.49) * mm, "end": v(214.93, 69.84) * mm});
            skLineSegment(sketch, "E57.6.36.0", {"start": v(210.22, 61.28) * mm, "end": v(217, 63.49) * mm});
            skLineSegment(sketch, "E57.9.36.0", {"start": v(208.15, 67.63) * mm, "end": v(210.22, 61.28) * mm});
            skLineSegment(sketch, "E57.12.36.0", {"start": v(208.15, 67.63) * mm, "end": v(206.1, 73.98) * mm});
            skLineSegment(sketch, "E57.15.36.0", {"start": v(206.1, 73.98) * mm, "end": v(212.87, 76.18) * mm});
            skLineSegment(sketch, "E57.1.37.0", {"start": v(200.2, 105.07) * mm, "end": v(203.12, 99.07) * mm});
            skLineSegment(sketch, "E57.3.37.0", {"start": v(206.05, 93.07) * mm, "end": v(203.12, 99.07) * mm});
            skLineSegment(sketch, "E57.6.37.0", {"start": v(199.64, 89.94) * mm, "end": v(206.05, 93.07) * mm});
            skLineSegment(sketch, "E57.9.37.0", {"start": v(196.71, 95.94) * mm, "end": v(199.64, 89.94) * mm});
            skLineSegment(sketch, "E57.12.37.0", {"start": v(196.71, 95.94) * mm, "end": v(193.79, 101.94) * mm});
            skLineSegment(sketch, "E57.15.37.0", {"start": v(193.79, 101.94) * mm, "end": v(200.2, 105.07) * mm});
            skLineSegment(sketch, "E57.1.38.0", {"start": v(183.62, 131.9) * mm, "end": v(187.36, 126.37) * mm});
            skLineSegment(sketch, "E57.3.38.0", {"start": v(191.09, 120.84) * mm, "end": v(187.36, 126.37) * mm});
            skLineSegment(sketch, "E57.6.38.0", {"start": v(185.18, 116.85) * mm, "end": v(191.09, 120.84) * mm});
            skLineSegment(sketch, "E57.9.38.0", {"start": v(181.45, 122.39) * mm, "end": v(185.18, 116.85) * mm});
            skLineSegment(sketch, "E57.12.38.0", {"start": v(181.45, 122.39) * mm, "end": v(177.71, 127.92) * mm});
            skLineSegment(sketch, "E57.15.38.0", {"start": v(177.71, 127.92) * mm, "end": v(183.62, 131.9) * mm});
            skLineSegment(sketch, "E57.1.39.0", {"start": v(163.48, 156.18) * mm, "end": v(167.95, 151.22) * mm});
            skLineSegment(sketch, "E57.3.39.0", {"start": v(172.41, 146.26) * mm, "end": v(167.95, 151.22) * mm});
            skLineSegment(sketch, "E57.6.39.0", {"start": v(167.12, 141.49) * mm, "end": v(172.41, 146.26) * mm});
            skLineSegment(sketch, "E57.9.39.0", {"start": v(162.65, 146.45) * mm, "end": v(167.12, 141.49) * mm});
            skLineSegment(sketch, "E57.12.39.0", {"start": v(162.65, 146.45) * mm, "end": v(158.18, 151.4) * mm});
            skLineSegment(sketch, "E57.15.39.0", {"start": v(158.18, 151.4) * mm, "end": v(163.48, 156.18) * mm});
            skLineSegment(sketch, "E57.1.40.0", {"start": v(140.15, 177.41) * mm, "end": v(145.27, 173.12) * mm});
            skLineSegment(sketch, "E57.3.40.0", {"start": v(150.38, 168.83) * mm, "end": v(145.27, 173.12) * mm});
            skLineSegment(sketch, "E57.6.40.0", {"start": v(145.8, 163.37) * mm, "end": v(150.38, 168.83) * mm});
            skLineSegment(sketch, "E57.9.40.0", {"start": v(140.68, 167.66) * mm, "end": v(145.8, 163.37) * mm});
            skLineSegment(sketch, "E57.12.40.0", {"start": v(140.68, 167.66) * mm, "end": v(135.57, 171.95) * mm});
            skLineSegment(sketch, "E57.15.40.0", {"start": v(135.57, 171.95) * mm, "end": v(140.15, 177.41) * mm});
            skLineSegment(sketch, "E57.1.41.0", {"start": v(114.1, 195.2) * mm, "end": v(119.76, 191.65) * mm});
            skLineSegment(sketch, "E57.3.41.0", {"start": v(125.42, 188.12) * mm, "end": v(119.76, 191.65) * mm});
            skLineSegment(sketch, "E57.6.41.0", {"start": v(121.64, 182.07) * mm, "end": v(125.42, 188.12) * mm});
            skLineSegment(sketch, "E57.9.41.0", {"start": v(115.98, 185.6) * mm, "end": v(121.64, 182.07) * mm});
            skLineSegment(sketch, "E57.12.41.0", {"start": v(115.98, 185.6) * mm, "end": v(110.32, 189.15) * mm});
            skLineSegment(sketch, "E57.15.41.0", {"start": v(110.32, 189.15) * mm, "end": v(114.1, 195.2) * mm});
            skLineSegment(sketch, "E57.1.42.0", {"start": v(85.82, 209.17) * mm, "end": v(91.92, 206.46) * mm});
            skLineSegment(sketch, "E57.3.42.0", {"start": v(98.02, 203.74) * mm, "end": v(91.92, 206.46) * mm});
            skLineSegment(sketch, "E57.6.42.0", {"start": v(95.12, 197.23) * mm, "end": v(98.02, 203.74) * mm});
            skLineSegment(sketch, "E57.9.42.0", {"start": v(89.02, 199.94) * mm, "end": v(95.12, 197.23) * mm});
            skLineSegment(sketch, "E57.12.42.0", {"start": v(89.02, 199.94) * mm, "end": v(82.92, 202.66) * mm});
            skLineSegment(sketch, "E57.15.42.0", {"start": v(82.92, 202.66) * mm, "end": v(85.82, 209.17) * mm});
            skLineSegment(sketch, "E57.1.43.0", {"start": v(55.88, 219.08) * mm, "end": v(62.3, 217.24) * mm});
            skLineSegment(sketch, "E57.3.43.0", {"start": v(68.7, 215.4) * mm, "end": v(62.3, 217.24) * mm});
            skLineSegment(sketch, "E57.6.43.0", {"start": v(66.74, 208.55) * mm, "end": v(68.7, 215.4) * mm});
            skLineSegment(sketch, "E57.9.43.0", {"start": v(60.33, 210.39) * mm, "end": v(66.74, 208.55) * mm});
            skLineSegment(sketch, "E57.12.43.0", {"start": v(60.33, 210.39) * mm, "end": v(53.91, 212.23) * mm});
            skLineSegment(sketch, "E57.15.43.0", {"start": v(53.91, 212.23) * mm, "end": v(55.88, 219.08) * mm});
            skLineSegment(sketch, "E57.1.44.0", {"start": v(24.84, 224.72) * mm, "end": v(31.45, 223.8) * mm});
            skLineSegment(sketch, "E57.3.44.0", {"start": v(38.06, 222.86) * mm, "end": v(31.45, 223.8) * mm});
            skLineSegment(sketch, "E57.6.44.0", {"start": v(37.07, 215.8) * mm, "end": v(38.06, 222.86) * mm});
            skLineSegment(sketch, "E57.9.44.0", {"start": v(30.46, 216.73) * mm, "end": v(37.07, 215.8) * mm});
            skLineSegment(sketch, "E57.12.44.0", {"start": v(30.46, 216.73) * mm, "end": v(23.85, 217.66) * mm});
            skLineSegment(sketch, "E57.15.44.0", {"start": v(23.85, 217.66) * mm, "end": v(24.84, 224.72) * mm});
            skSolve(sketch);
        }
        {
            var Q0;
            Q0 = qSketchRegion(id + "F5", true);
            extrude(context, id + "F6", {"entities" : qUnion([Q0]), "operationType" : NewBodyOperationType.REMOVE, "oppositeDirection" : true, "depth" : 6.35 * mm});
        }
    });
